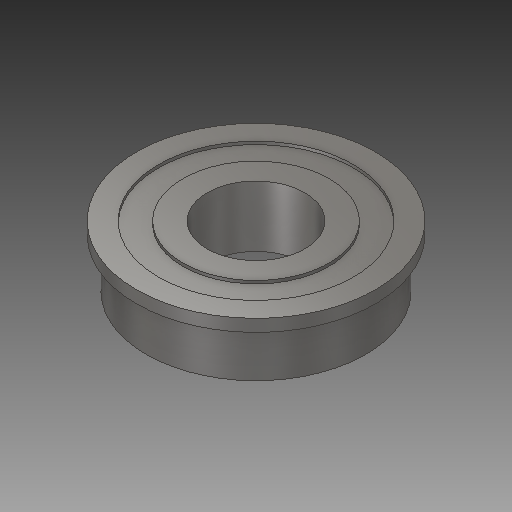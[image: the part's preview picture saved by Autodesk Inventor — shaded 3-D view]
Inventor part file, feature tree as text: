
AUTODESK INVENTOR PART (.ipt)
format: ipt  version: 2017 (Build 210142000, 142)  size: 145,920 bytes
history: native  units: in
note: dims shown in document units (in); Inventor stores cm internally (conversion verified against a paired STEP export)
features: revolve x1
ambient origin geometry x8: Origin, YZ Plane, XZ Plane, XY Plane, X Axis, Y Axis, Z Axis, Center Point
bodies: Solid1 (feature_tree)
feature tree (1):
  revolve  "Revolve1"  [1 undecoded]
note: 1 required parameter value undecoded (feature->parameter linkage not recoverable at this tier; creation-order binding heuristic only, values carry confidence <= 0.55)
